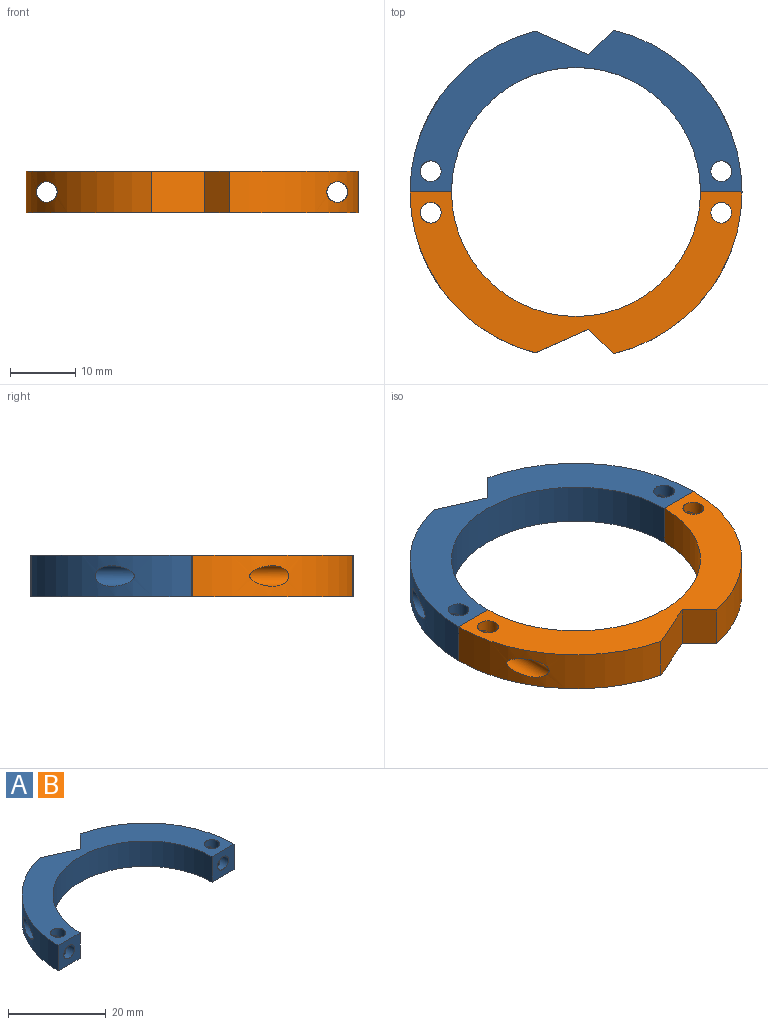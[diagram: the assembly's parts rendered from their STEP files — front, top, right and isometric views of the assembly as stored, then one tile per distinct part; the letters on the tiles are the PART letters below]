
ASSEMBLY  parts=2 mates=1
PART A: 17 faces, bbox 50.8x24.8x6.4 mm
  f0: cylinder r=1.59mm len=11.63mm, axis (0,-1,0), area 78.6mm2, adj f4,f15,f16
  f1: cylinder r=1.59mm len=3.18mm, axis (0,-1,0), area 21.6mm2, adj f3,f15,f16
  f2: cylinder r=1.59mm len=3.18mm, axis (0,-1,0), area 21.6mm2, adj f8,f13,f14
  f3: plane 6.35x6.35mm, normal (0,-1,0), area 32.4mm2, adj f1,f4,f9,f10,f11
  f4: cylinder r=25.4mm len=24.76mm, axis (0,0,-1), area 200.4mm2, adj f0,f3,f5,f10,f11
  f5: plane 6.35x3.76mm, normal (-0.71,0.7,0), area 33.6mm2, adj f4,f6,f10,f11
  f6: plane 8.2x6.35mm, normal (0.4,0.91,0), area 56.9mm2, adj f5,f7,f10,f11
  f7: cylinder r=25.4mm len=24.62mm, axis (0,0,-1), area 196.7mm2, adj f6,f8,f10,f11,f12
  f8: plane 6.35x6.35mm, normal (0,-1,0), area 32.4mm2, adj f2,f7,f9,f10,f11
  f9: cylinder r=19.05mm len=38.1mm, axis (0,0,-1), area 380mm2, adj f3,f8,f10,f11
  f10: plane 50.8x24.76mm, normal (0,0,1), area 399.8mm2, adj f3,f4,f5,f6,f7,f8,f9,f13
  f11: plane 50.8x24.76mm, normal (0,0,-1), area 399.8mm2, adj f3,f4,f5,f6,f7,f8,f9,f14
  f12: cylinder r=1.59mm len=11.63mm, axis (0,-1,0), area 78.6mm2, adj f7,f13,f14
  f13: cylinder r=1.59mm len=3.18mm, axis (0,0,1), area 21.6mm2, adj f2,f10,f12
  f14: cylinder r=1.59mm len=3.18mm, axis (0,0,1), area 21.6mm2, adj f2,f11,f12
  f15: cylinder r=1.59mm len=3.18mm, axis (0,0,1), area 21.6mm2, adj f0,f1,f11
  f16: cylinder r=1.59mm len=3.18mm, axis (0,0,1), area 21.6mm2, adj f0,f1,f10
PART B: same geometry as A
PLACE A t=(-30.51,-3.77,-10.85)mm
PLACE B rot(axis=(-1,0,0),180deg) t=(-30.51,-3.77,-4.5)mm
MATE cylindrical A.f2 <-> B.f2  axis (0,-1,0) through (-52.73,-3.77,-7.68)mm
